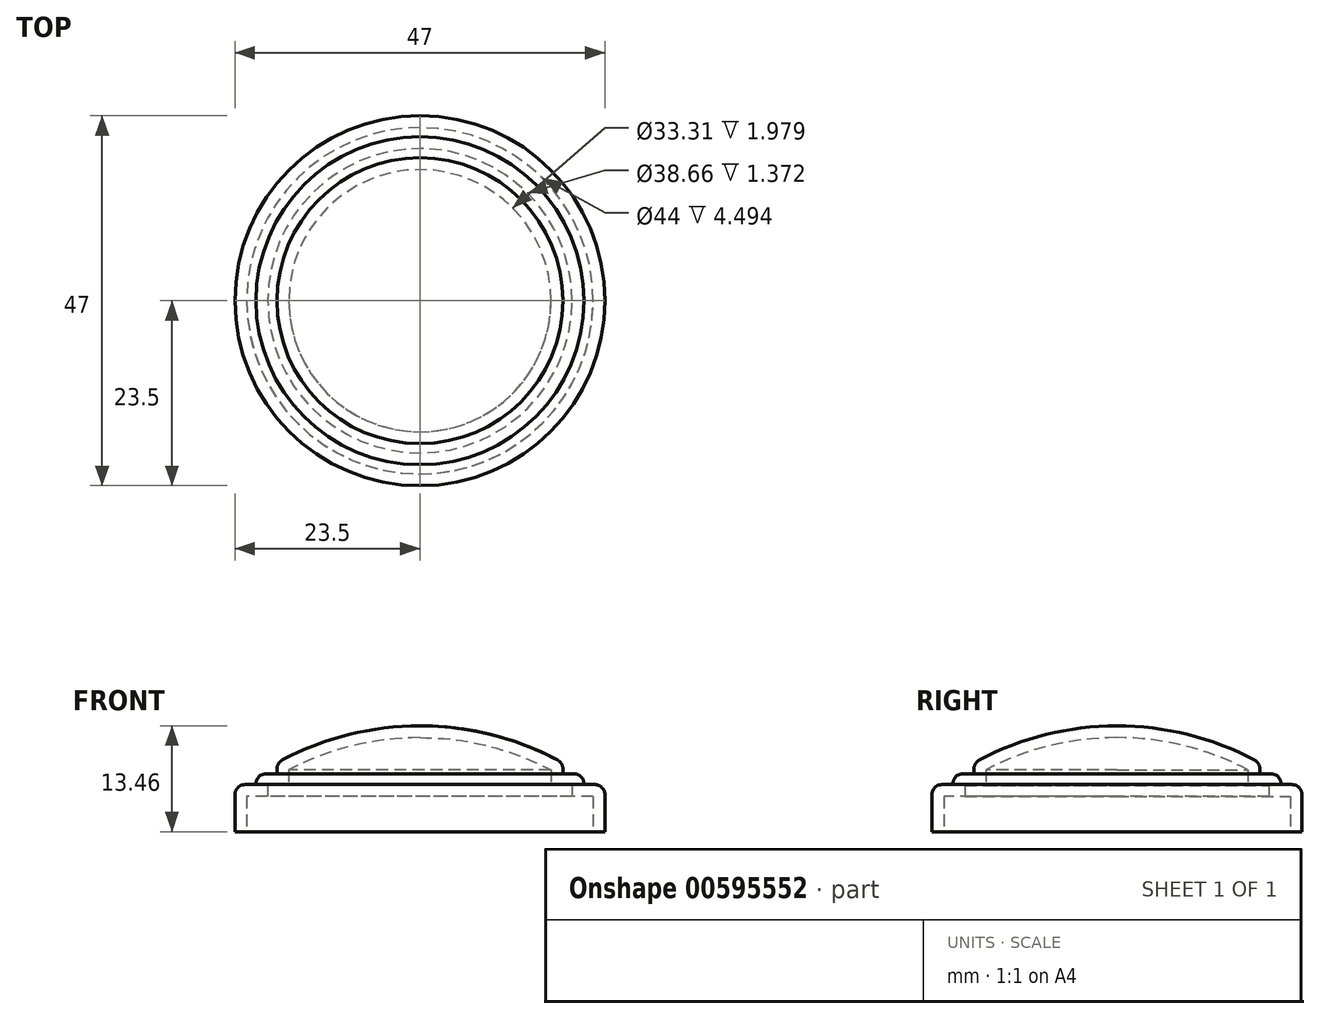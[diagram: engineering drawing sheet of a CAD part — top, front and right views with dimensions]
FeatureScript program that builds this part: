
annotation { "Feature Type Name" : "Feature", "Feature Type Description" : "" }
export const myFeature = defineFeature(function(context is Context, id is Id, definition is map)
    precondition{}
    {
        {
            var Q0;
            Q0=qCreatedBy(makeId("Front.planeOp"),FACE);
            var sketch = newSketch(context, id + "F0", { "sketchPlane" : qUnion([Q0])});
            skLineSegment(sketch, "E0", {"start": v(0, 0) * mm, "end": v(0, 13.46) * mm});
            skLineSegment(sketch, "E1", {"start": v(0, 0) * mm, "end": v(-23.5, 0) * mm});
            skLineSegment(sketch, "E2", {"start": v(-23.5, 0) * mm, "end": v(-23.5, 6) * mm});
            skLineSegment(sketch, "E3", {"start": v(-23.5, 6) * mm, "end": v(0, 6) * mm});
            skLineSegment(sketch, "E4", {"start": v(-20.83, 6) * mm, "end": v(-20.83, 7.37) * mm});
            skLineSegment(sketch, "E5", {"start": v(-20.83, 7.37) * mm, "end": v(0, 7.37) * mm});
            skLineSegment(sketch, "E6", {"start": v(-18.16, 7.37) * mm, "end": v(-18.16, 8.74) * mm});
            skArc(sketch, "E7", {"start": v(0, 13.46) * mm, "mid": v(-9.38, 12.26) * mm, "end": v(-18.16, 8.74) * mm});
            skLineSegment(sketch, "E8", {"start": v(0, 13.46) * mm, "end": v(6.18, 13.46) * mm, "construction": true});
            skSolve(sketch);
        }
        {
            var Q0;
            {var subQ1=sQuery(id+"F0.wireOp",EDGE,"E1");Q0=makeQuery(id+"F0.imprint","IMPRINT",FACE,{"disambiguationData":[TD([[makeQuery(id+"F0.imprint","IMPRINT",EDGE,{"derivedFrom":subQ1}),-1.0]])]});}
            var Q1;
            {var subQ1=sQuery(id+"F0.wireOp",EDGE,"E4");Q1=makeQuery(id+"F0.imprint","IMPRINT",FACE,{"disambiguationData":[TD([[makeQuery(id+"F0.imprint","IMPRINT",EDGE,{"derivedFrom":subQ1}),-1.0]])]});}
            var Q2;
            {var subQ4=sQuery(id+"F0.wireOp",EDGE,"E6");Q2=makeQuery(id+"F0.imprint","IMPRINT",FACE,{"disambiguationData":[TD([[makeQuery(id+"F0.imprint","IMPRINT",EDGE,{"derivedFrom":subQ4}),-1.0]])]});}
            var Q3;
            Q3=sQuery(id+"F0.wireOp",EDGE,"E0");
            revolve(context, id + "F1", {"entities" : qUnion([Q0, Q1, Q2]), "axis" : qUnion([Q3]), "revolveType" : RevolveType.FULL});
        }
        {
            var Q0;
            Q0=makeQuery(id+"F1.opRevolve","SWEPT_EDGE",EDGE,{"disambiguationData":[OSD([sQuery(id+"F0.wireOp",EDGE,"E4"),sQuery(id+"F0.wireOp",EDGE,"E5")])]});
            var Q1;
            Q1=makeQuery(id+"F1.opRevolve","SWEPT_EDGE",EDGE,{"disambiguationData":[OSD([sQuery(id+"F0.wireOp",EDGE,"E6"),sQuery(id+"F0.wireOp",EDGE,"E7")])]});
            var Q2;
            Q2=makeQuery(id+"F1.opRevolve","SWEPT_EDGE",EDGE,{"disambiguationData":[OSD([sQuery(id+"F0.wireOp",EDGE,"E2"),sQuery(id+"F0.wireOp",EDGE,"E3")])]});
            fillet(context, id + "F2", {"entities" : qUnion([Q0, Q1, Q2]), "radius" : 1.27 * mm, "tangentPropagation" : true, "allowEdgeOverflow" : false});
        }
        {
            var Q0;
            Q0=makeQuery(id+"F1.opRevolve","SWEPT_FACE",FACE,{"disambiguationData":[OSD([sQuery(id+"F0.wireOp",EDGE,"E1")])]});
            shell(context, id + "F3", {"entities" : qUnion([Q0]), "thickness" : 1.5 * mm});
        }
    });
